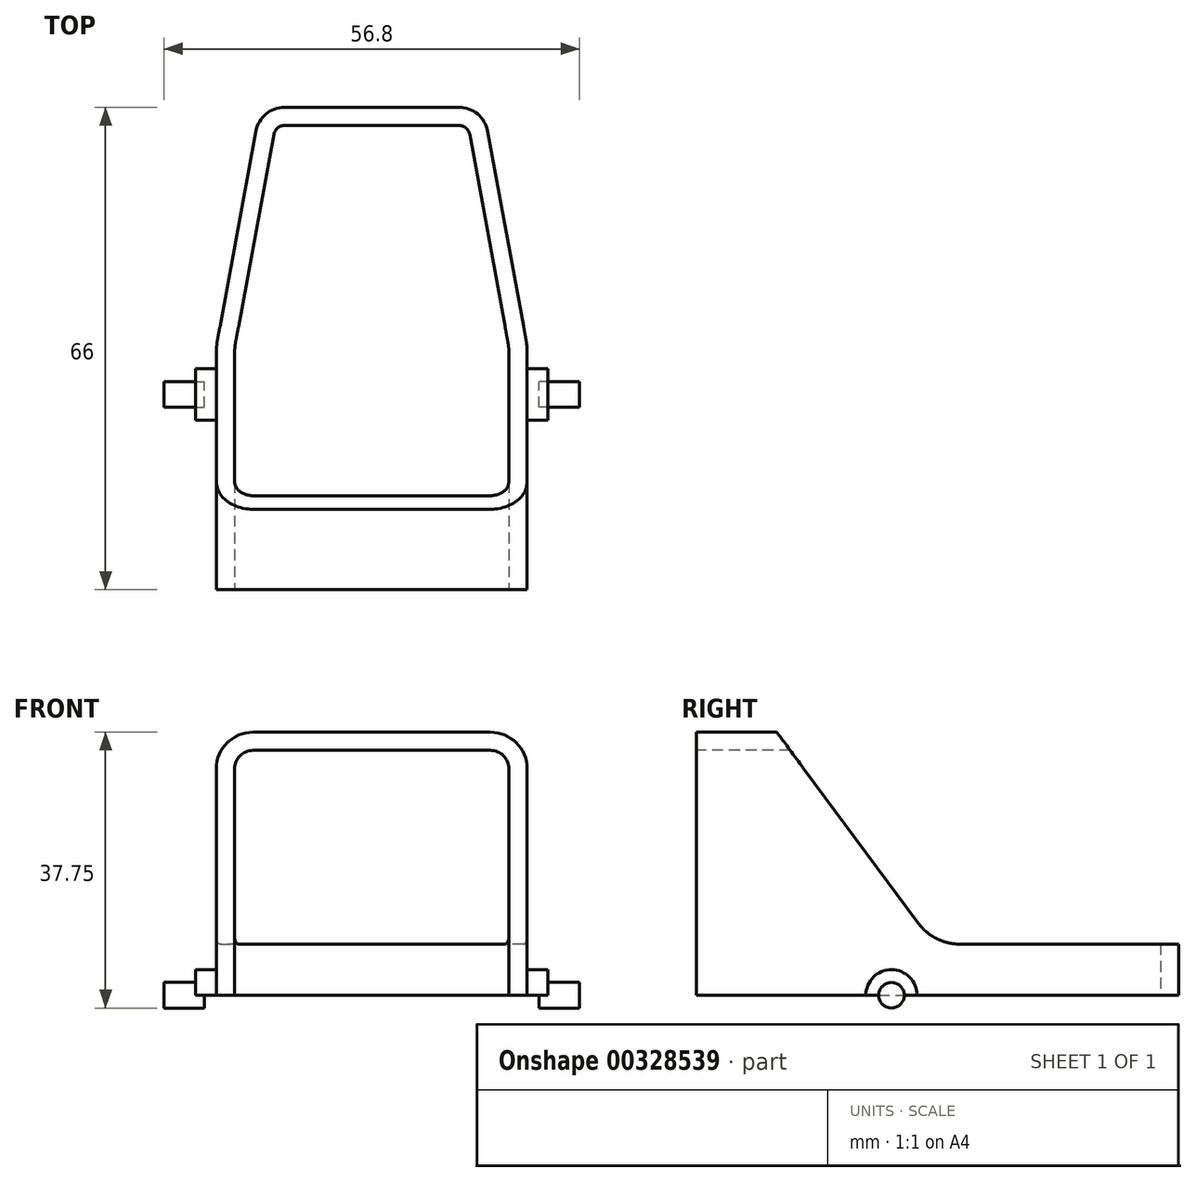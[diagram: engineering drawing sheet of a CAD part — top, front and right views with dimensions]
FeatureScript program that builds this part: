
annotation { "Feature Type Name" : "Feature", "Feature Type Description" : "" }
export const myFeature = defineFeature(function(context is Context, id is Id, definition is map)
    precondition{}
    {
        {
            var Q0;
            Q0=qCreatedBy(makeId("Top.planeOp"),FACE);
            var sketch = newSketch(context, id + "F0", { "sketchPlane" : qUnion([Q0])});
            skLineSegment(sketch, "E0", {"start": v(-21.25, 0) * mm, "end": v(-21.25, 32.5) * mm});
            skLineSegment(sketch, "E1", {"start": v(-21.08, 34.31) * mm, "end": v(-15.85, 62.72) * mm});
            skLineSegment(sketch, "E2", {"start": v(-11.92, 66) * mm, "end": v(0, 66) * mm});
            skPoint(sketch, "E3.visualSharp", {"position": v(-15.25, 66) * mm});
            skArc(sketch, "E3.filletArc", {"start": v(-11.92, 66) * mm, "mid": v(-14.48, 65.07) * mm, "end": v(-15.85, 62.72) * mm});
            skPoint(sketch, "E4.visualSharp", {"position": v(-21.25, 33.41) * mm});
            skArc(sketch, "E4.filletArc", {"start": v(-21.08, 34.31) * mm, "mid": v(-21.2, 33.4) * mm, "end": v(-21.25, 32.5) * mm});
            skLineSegment(sketch, "E5.0", {"start": v(-11.92, 63.5) * mm, "end": v(0, 63.5) * mm});
            skLineSegment(sketch, "E5.1", {"start": v(-18.75, 0) * mm, "end": v(-18.75, 32.5) * mm});
            skArc(sketch, "E5.2", {"start": v(-18.63, 33.86) * mm, "mid": v(-18.72, 33.18) * mm, "end": v(-18.75, 32.5) * mm});
            skLineSegment(sketch, "E5.3", {"start": v(-18.63, 33.86) * mm, "end": v(-13.4, 62.27) * mm});
            skArc(sketch, "E5.4", {"start": v(-11.92, 63.5) * mm, "mid": v(-12.88, 63.15) * mm, "end": v(-13.4, 62.27) * mm});
            skLineSegment(sketch, "E6", {"start": v(-18.75, 0) * mm, "end": v(-21.25, 0) * mm});
            skLineSegment(sketch, "E7", {"start": v(0, 0) * mm, "end": v(0, 81.25) * mm, "construction": true});
            skArc(sketch, "E8.MirrorCS", {"start": v(18.63, 33.86) * mm, "mid": v(18.72, 33.18) * mm, "end": v(18.75, 32.5) * mm});
            skLineSegment(sketch, "E9.MirrorCS", {"start": v(18.75, 0) * mm, "end": v(21.25, 0) * mm});
            skArc(sketch, "E10.MirrorCS", {"start": v(21.08, 34.31) * mm, "mid": v(21.2, 33.4) * mm, "end": v(21.25, 32.5) * mm});
            skLineSegment(sketch, "E11.MirrorCS", {"start": v(21.25, 0) * mm, "end": v(21.25, 32.5) * mm});
            skPoint(sketch, "E12.MirrorP", {"position": v(15.25, 66) * mm});
            skLineSegment(sketch, "E13.MirrorCS", {"start": v(18.63, 33.86) * mm, "end": v(13.4, 62.27) * mm});
            skLineSegment(sketch, "E14.MirrorCS", {"start": v(18.75, 0) * mm, "end": v(18.75, 32.5) * mm});
            skArc(sketch, "E15.MirrorCS", {"start": v(11.92, 66) * mm, "mid": v(14.48, 65.07) * mm, "end": v(15.85, 62.72) * mm});
            skArc(sketch, "E16.MirrorCS", {"start": v(11.92, 63.5) * mm, "mid": v(12.88, 63.15) * mm, "end": v(13.4, 62.27) * mm});
            skLineSegment(sketch, "E17.MirrorCS", {"start": v(11.92, 66) * mm, "end": v(0, 66) * mm});
            skLineSegment(sketch, "E18.MirrorCS", {"start": v(11.92, 63.5) * mm, "end": v(0, 63.5) * mm});
            skLineSegment(sketch, "E19.MirrorCS", {"start": v(21.08, 34.31) * mm, "end": v(15.85, 62.72) * mm});
            skPoint(sketch, "E20.MirrorP", {"position": v(21.25, 33.41) * mm});
            skSolve(sketch);
        }
        {
            var Q0;
            Q0 = qSketchRegion(id + "F0", true);
            extrude(context, id + "F1", {"entities" : qUnion([Q0]), "depth" : 7 * mm});
        }
        {
            var Q0;
            Q0=makeQuery(id+"F1.opExtrude","SWEPT_FACE",FACE,{"disambiguationData":[OSD([sQuery(id+"F0.wireOp",EDGE,"E6")])]});
            var sketch = newSketch(context, id + "F2", { "sketchPlane" : qUnion([Q0])});
            skLineSegment(sketch, "E21", {"start": v(-21.25, 7) * mm, "end": v(-21.25, 31) * mm});
            skLineSegment(sketch, "E22", {"start": v(-16.25, 36) * mm, "end": v(0, 36) * mm});
            skPoint(sketch, "E23.visualSharp", {"position": v(-21.25, 36) * mm});
            skArc(sketch, "E23.filletArc", {"start": v(-16.25, 36) * mm, "mid": v(-19.79, 34.54) * mm, "end": v(-21.25, 31) * mm});
            skLineSegment(sketch, "E24", {"start": v(-18.75, 7) * mm, "end": v(-18.75, 31) * mm});
            skLineSegment(sketch, "E25", {"start": v(-16.25, 33.5) * mm, "end": v(0, 33.5) * mm});
            skLineSegment(sketch, "E26", {"start": v(0, 36) * mm, "end": v(0, 33.5) * mm, "construction": true});
            skPoint(sketch, "E27.visualSharp", {"position": v(-18.75, 33.5) * mm});
            skArc(sketch, "E27.filletArc", {"start": v(-16.25, 33.5) * mm, "mid": v(-18.02, 32.77) * mm, "end": v(-18.75, 31) * mm});
            skLineSegment(sketch, "E28", {"start": v(-21.25, 7) * mm, "end": v(-18.75, 7) * mm});
            skLineSegment(sketch, "E29.MirrorCS", {"start": v(21.25, 7) * mm, "end": v(18.75, 7) * mm});
            skLineSegment(sketch, "E30.MirrorCS", {"start": v(18.75, 7) * mm, "end": v(18.75, 31) * mm});
            skLineSegment(sketch, "E31.MirrorCS", {"start": v(21.25, 7) * mm, "end": v(21.25, 31) * mm});
            skArc(sketch, "E32.MirrorCS", {"start": v(16.25, 33.5) * mm, "mid": v(18.02, 32.77) * mm, "end": v(18.75, 31) * mm});
            skArc(sketch, "E33.MirrorCS", {"start": v(16.25, 36) * mm, "mid": v(19.79, 34.54) * mm, "end": v(21.25, 31) * mm});
            skLineSegment(sketch, "E34.MirrorCS", {"start": v(16.25, 36) * mm, "end": v(0, 36) * mm});
            skLineSegment(sketch, "E35.MirrorCS", {"start": v(16.25, 33.5) * mm, "end": v(0, 33.5) * mm});
            skSolve(sketch);
        }
        {
            var Q0;
            Q0 = qSketchRegion(id + "F2", true);
            var Q1;
            Q1=makeQuery(id+"F1.opExtrude","CAP_VERTEX",VERTEX,{"disambiguationData":[OSD([sQuery(id+"F0.wireOp",EDGE,"E10.MirrorCS"),sQuery(id+"F0.wireOp",EDGE,"E11.MirrorCS")])],"isStart":false});
            extrude(context, id + "F3", {"entities" : qUnion([Q0]), "operationType" : NewBodyOperationType.ADD, "endBound" : BoundingType.UP_TO_VERTEX, "oppositeDirection" : true, "endBoundEntityVertex" : qUnion([Q1]), "depth" : 25 * mm});
        }
        {
            var Q0;
            Q0=makeQuery(id+"F3.boolean.opBoolean","MERGE",FACE,{"derivedFrom":[makeQuery(id+"F1.opExtrude","SWEPT_FACE",FACE,{"disambiguationData":[OSD([sQuery(id+"F0.wireOp",EDGE,"E11.MirrorCS")])]}),makeQuery(id+"F3.opExtrude","SWEPT_FACE",FACE,{"disambiguationData":[OSD([sQuery(id+"F2.wireOp",EDGE,"E31.MirrorCS")])]})]});
            var sketch = newSketch(context, id + "F4", { "sketchPlane" : qUnion([Q0])});
            skLineSegment(sketch, "E36", {"start": v(32.5, 7) * mm, "end": v(11, 36) * mm});
            skLineSegment(sketch, "E37", {"start": v(11, 36) * mm, "end": v(32.5, 36) * mm});
            skLineSegment(sketch, "E38", {"start": v(32.5, 36) * mm, "end": v(32.5, 7) * mm});
            skSolve(sketch);
        }
        {
            var Q0;
            Q0 = qSketchRegion(id + "F4", true);
            extrude(context, id + "F5", {"entities" : qUnion([Q0]), "operationType" : NewBodyOperationType.REMOVE, "endBound" : BoundingType.THROUGH_ALL, "oppositeDirection" : true, "depth" : 25 * mm});
        }
        {
            var Q0;
            Q0=makeQuery(id+"F3.boolean.opBoolean","MERGE",FACE,{"derivedFrom":[makeQuery(id+"F1.opExtrude","SWEPT_FACE",FACE,{"disambiguationData":[OSD([sQuery(id+"F0.wireOp",EDGE,"E11.MirrorCS")])]}),makeQuery(id+"F3.opExtrude","SWEPT_FACE",FACE,{"disambiguationData":[OSD([sQuery(id+"F2.wireOp",EDGE,"E31.MirrorCS")])]})]});
            var sketch = newSketch(context, id + "F6", { "sketchPlane" : qUnion([Q0])});
            skArc(sketch, "E39", {"start": v(30.2, 0) * mm, "mid": v(26.7, 3.5) * mm, "end": v(23.2, 0) * mm});
            skLineSegment(sketch, "E40", {"start": v(23.2, 0) * mm, "end": v(30.2, 0) * mm});
            skSolve(sketch);
        }
        {
            var Q0;
            Q0 = qSketchRegion(id + "F6", true);
            extrude(context, id + "F7", {"entities" : qUnion([Q0]), "operationType" : NewBodyOperationType.ADD, "depth" : 2.85 * mm});
        }
        {
            var Q0;
            Q0=makeQuery(id+"F7.opExtrude","CAP_FACE",FACE,{"disambiguationData":[OSD([sQuery(id+"F6.wireOp",EDGE,"E39")])],"isStart":false});
            var sketch = newSketch(context, id + "F8", { "sketchPlane" : qUnion([Q0])});
            skCircle(sketch, "E41", {"center": v(26.7, 0) * mm, "radius": 1.75 * mm});
            skSolve(sketch);
        }
        {
            var Q0;
            Q0 = qSketchRegion(id + "F8", true);
            extrude(context, id + "F9", {"entities" : qUnion([Q0]), "operationType" : NewBodyOperationType.ADD, "flatOperationType" : FlatOperationType.REMOVE, "offsetDistance" : 25 * mm, "depth" : 4.3 * mm, "hasSecondDirection" : true, "secondDirectionOppositeDirection" : true, "secondDirectionDepth" : 1.2 * mm, "domain" : OperationDomain.MODEL});
        }
        {
            var Q0;
            Q0=makeQuery(id+"F1.opExtrude","SWEPT_BODY",BODY,{"disambiguationData":[OSD([sQuery(id+"F0.wireOp",EDGE,"E0"),sQuery(id+"F0.wireOp",EDGE,"E1"),sQuery(id+"F0.wireOp",EDGE,"E2"),sQuery(id+"F0.wireOp",EDGE,"E3.filletArc"),sQuery(id+"F0.wireOp",EDGE,"E4.filletArc"),sQuery(id+"F0.wireOp",EDGE,"E5.0"),sQuery(id+"F0.wireOp",EDGE,"E5.1"),sQuery(id+"F0.wireOp",EDGE,"E5.2"),sQuery(id+"F0.wireOp",EDGE,"E5.3"),sQuery(id+"F0.wireOp",EDGE,"E5.4"),sQuery(id+"F0.wireOp",EDGE,"E6"),sQuery(id+"F0.wireOp",EDGE,"E8.MirrorCS"),sQuery(id+"F0.wireOp",EDGE,"E9.MirrorCS"),sQuery(id+"F0.wireOp",EDGE,"E10.MirrorCS"),sQuery(id+"F0.wireOp",EDGE,"E11.MirrorCS"),sQuery(id+"F0.wireOp",EDGE,"E13.MirrorCS"),sQuery(id+"F0.wireOp",EDGE,"E14.MirrorCS"),sQuery(id+"F0.wireOp",EDGE,"E15.MirrorCS"),sQuery(id+"F0.wireOp",EDGE,"E16.MirrorCS"),sQuery(id+"F0.wireOp",EDGE,"E17.MirrorCS"),sQuery(id+"F0.wireOp",EDGE,"E18.MirrorCS"),sQuery(id+"F0.wireOp",EDGE,"E19.MirrorCS")])]});
            var Q1;
            Q1=qCreatedBy(makeId("Right.planeOp"),FACE);
            mirror(context, id + "F10", {"operationType" : NewBodyOperationType.ADD, "entities" : qUnion([Q0]), "mirrorPlane" : qUnion([Q1])});
        }
        {
            var Q0;
            Q0=makeQuery(id+"F5.boolean.opBoolean","MERGE",EDGE,{"derivedFrom":[makeQuery(id+"F3.opExtrude","CAP_EDGE",EDGE,{"disambiguationData":[OSD([sQuery(id+"F2.wireOp",EDGE,"E28")])],"isStart":false})],"fromTools":[makeQuery(id+"F5.opExtrude","SWEPT_EDGE",EDGE,{"disambiguationData":[OSD([sQuery(id+"F0.wireOp",EDGE,"E10.MirrorCS"),sQuery(id+"F0.wireOp",EDGE,"E11.MirrorCS"),sQuery(id+"F4.wireOp",EDGE,"E36"),sQuery(id+"F4.wireOp",EDGE,"E38")])]})]});
            var Q1;
            Q1=makeQuery(id+"F5.boolean.opBoolean","MERGE",EDGE,{"derivedFrom":[makeQuery(id+"F3.opExtrude","CAP_EDGE",EDGE,{"disambiguationData":[OSD([sQuery(id+"F2.wireOp",EDGE,"E29.MirrorCS")])],"isStart":false})],"fromTools":[makeQuery(id+"F5.opExtrude","SWEPT_EDGE",EDGE,{"disambiguationData":[OSD([sQuery(id+"F0.wireOp",EDGE,"E10.MirrorCS"),sQuery(id+"F0.wireOp",EDGE,"E11.MirrorCS"),sQuery(id+"F4.wireOp",EDGE,"E36"),sQuery(id+"F4.wireOp",EDGE,"E38")])]})]});
            fillet(context, id + "F11", {"entities" : qUnion([Q0, Q1]), "radius" : 7 * mm, "tangentPropagation" : true, "allowEdgeOverflow" : false});
        }
    });
